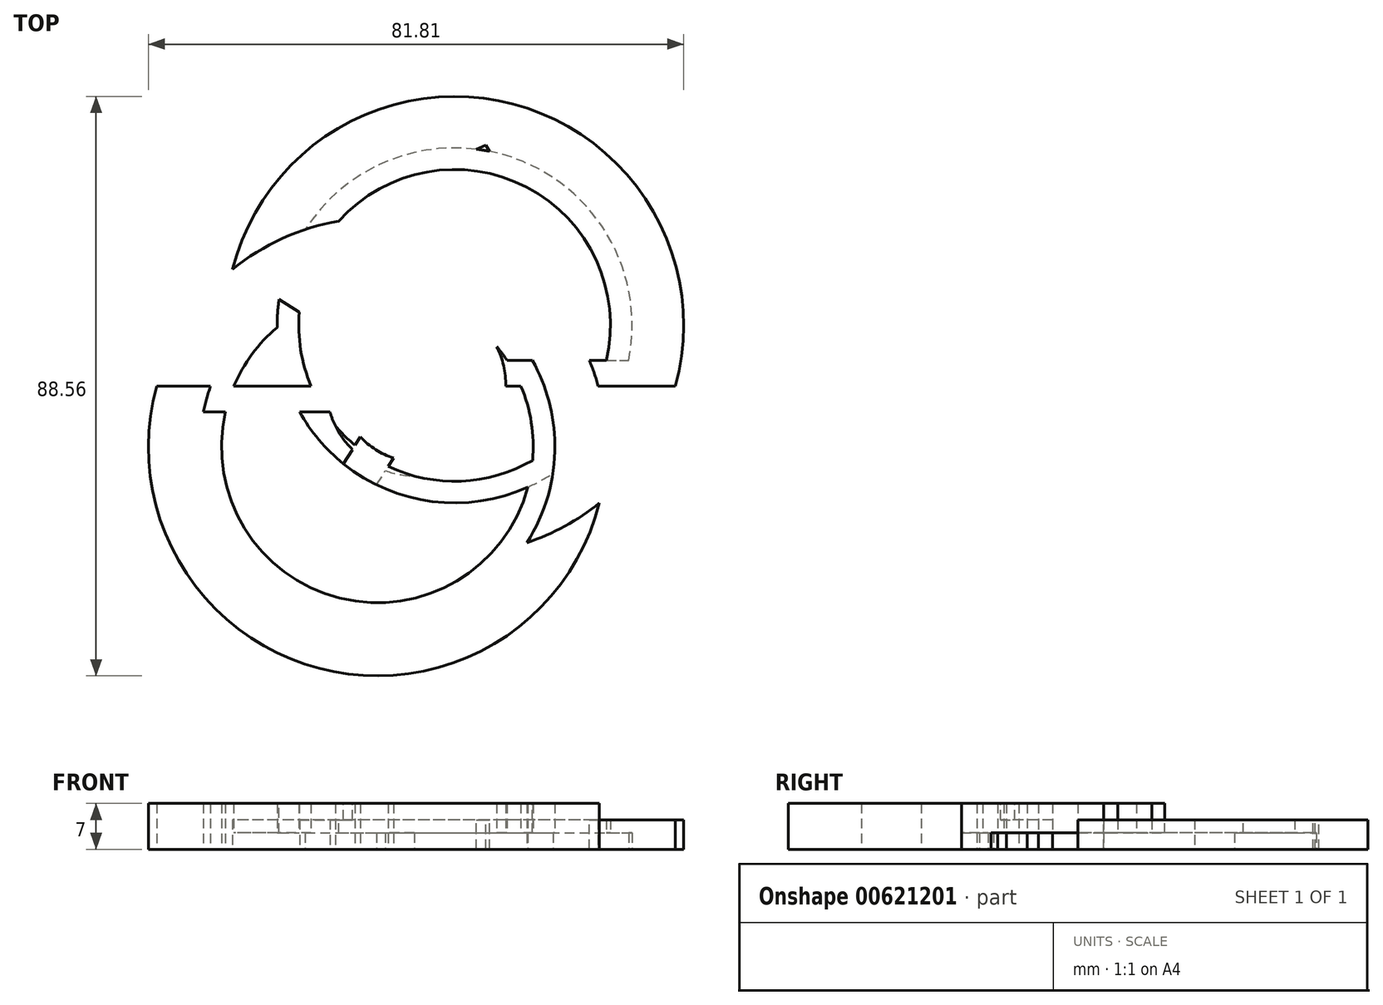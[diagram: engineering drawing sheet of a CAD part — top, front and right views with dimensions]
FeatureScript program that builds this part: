
annotation { "Feature Type Name" : "Feature", "Feature Type Description" : "" }
export const myFeature = defineFeature(function(context is Context, id is Id, definition is map)
    precondition{}
    {
        {
            var Q0;
            Q0=qCreatedBy(makeId("Top.planeOp"),FACE);
            var sketch = newSketch(context, id + "F0", { "sketchPlane" : qUnion([Q0])});
            skLineSegment(sketch, "E0", {"start": v(-39.07, 0) * mm, "end": v(40.23, 0) * mm});
            skPoint(sketch, "E1", {"position": v(0.58, 0) * mm});
            skPoint(sketch, "E2", {"position": v(11.92, 0) * mm});
            skPoint(sketch, "E3", {"position": v(-10.76, 0) * mm});
            skPoint(sketch, "E4", {"position": v(-22.57, 0) * mm});
            skArc(sketch, "E5", {"start": v(28.42, 0) * mm, "mid": v(-5.33, 25.72) * mm, "end": v(-39.07, 0) * mm});
            skLineSegment(sketch, "E6", {"start": v(28.42, 3.92) * mm, "end": v(40.23, 3.92) * mm});
            skPoint(sketch, "E7", {"position": v(34.32, 0) * mm});
            skPoint(sketch, "E7.positionSnap0", {"position": v(34.32, 3.92) * mm});
            skPoint(sketch, "E8", {"position": v(-30.82, 0) * mm});
            skPoint(sketch, "E9", {"position": v(-16.67, 0) * mm});
            skLineSegment(sketch, "E10", {"start": v(28.42, 3.92) * mm, "end": v(11.92, 3.92) * mm});
            skPoint(sketch, "E11", {"position": v(20.17, 0) * mm});
            skPoint(sketch, "E11.positionSnap0", {"position": v(20.17, 3.92) * mm});
            skArc(sketch, "E12", {"start": v(20.17, 0) * mm, "mid": v(-5.33, 17.85) * mm, "end": v(-30.82, 0) * mm});
            skLineSegment(sketch, "E13", {"start": v(40.23, 0) * mm, "end": v(-39.07, 0) * mm});
            skPoint(sketch, "E14", {"position": v(-27.27, 0) * mm});
            skPoint(sketch, "E15", {"position": v(23.72, 0) * mm});
            skArc(sketch, "E16", {"start": v(-27.27, 0) * mm, "mid": v(6.48, -25.72) * mm, "end": v(40.23, 0) * mm});
            skLineSegment(sketch, "E17", {"start": v(-27.27, -3.92) * mm, "end": v(-39.07, -3.92) * mm});
            skPoint(sketch, "E18", {"position": v(-33.17, 0) * mm});
            skPoint(sketch, "E18.positionSnap0", {"position": v(-33.17, -3.92) * mm});
            skPoint(sketch, "E19", {"position": v(31.98, 0) * mm});
            skPoint(sketch, "E20", {"position": v(24.15, -22) * mm});
            skLineSegment(sketch, "E21", {"start": v(-27.27, -3.92) * mm, "end": v(-10.76, -3.92) * mm});
            skPoint(sketch, "E22", {"position": v(-19.01, 0) * mm});
            skPoint(sketch, "E22.positionSnap0", {"position": v(-19.01, -3.92) * mm});
            skArc(sketch, "E23", {"start": v(-19.01, 0) * mm, "mid": v(6.48, -17.85) * mm, "end": v(31.98, 0) * mm});
            skCircle(sketch, "E24", {"center": v(6.48, 9.28) * mm, "radius": 27.13 * mm});
            skCircle(sketch, "E25", {"center": v(-5.33, -9.28) * mm, "radius": 27.13 * mm});
            skCircle(sketch, "E26", {"center": v(6.48, 9.28) * mm, "radius": 35 * mm});
            skCircle(sketch, "E27", {"center": v(-5.33, -9.28) * mm, "radius": 35 * mm});
            skLineSegment(sketch, "E28", {"start": v(0.58, 0) * mm, "end": v(-5.33, -9.28) * mm});
            skLineSegment(sketch, "E29", {"start": v(0.58, 0) * mm, "end": v(5.05, 7.03) * mm});
            skLineSegment(sketch, "E30", {"start": v(9.24, 13.61) * mm, "end": v(15.3, 9.75) * mm});
            skLineSegment(sketch, "E31", {"start": v(9.24, 13.61) * mm, "end": v(0.7, 19.04) * mm});
            skLineSegment(sketch, "E32", {"start": v(6.7, 15.22) * mm, "end": v(11.77, 12) * mm});
            skPoint(sketch, "E33", {"position": v(9.24, 13.61) * mm});
            skLineSegment(sketch, "E34", {"start": v(6.7, 15.22) * mm, "end": v(-10.53, -11.86) * mm});
            skLineSegment(sketch, "E35", {"start": v(11.77, 12) * mm, "end": v(-5.46, -15.08) * mm});
            skPoint(sketch, "E36", {"position": v(7.95, 11.59) * mm});
            skCircle(sketch, "E37", {"center": v(0.58, 0) * mm, "radius": 13.74 * mm});
            skCircle(sketch, "E38", {"center": v(-5.33, -9.28) * mm, "radius": 23.82 * mm});
            skCircle(sketch, "E39", {"center": v(6.48, 9.28) * mm, "radius": 23.82 * mm});
            skCircle(sketch, "E40", {"center": v(0.58, 0) * mm, "radius": 11.5 * mm});
            skSolve(sketch);
        }
        {
            var Q0;
            {var subQ0=sQuery(id+"F0.wireOp",EDGE,"E27");var subQ1=sQuery(id+"F0.wireOp",EDGE,"E13");var subQ2=makeQuery(id+"F0.imprint","INTERSECT",VERTEX,{"disambiguationData":[OD(0.0)],"derivedFrom":[subQ1,subQ0]});Q0=makeQuery(id+"F0.imprint","IMPRINT",FACE,{"disambiguationData":[TD([[makeQuery(id+"F0.imprint","IMPRINT",EDGE,{"disambiguationData":[TD([[subQ2,1.0]])],"derivedFrom":subQ1}),-1.0]])]});}
            var Q1;
            {var subQ0=sQuery(id+"F0.wireOp",EDGE,"E25");var subQ1=sQuery(id+"F0.wireOp",EDGE,"E24");var subQ2=makeQuery(id+"F0.imprint","INTERSECT",VERTEX,{"disambiguationData":[OD(0.0)],"derivedFrom":[subQ1,subQ0]});Q1=makeQuery(id+"F0.imprint","IMPRINT",FACE,{"disambiguationData":[TD([[makeQuery(id+"F0.imprint","IMPRINT",EDGE,{"disambiguationData":[TD([[subQ2,1.0]])],"derivedFrom":subQ1}),-1.0]])]});}
            var Q2;
            {var subQ0=sQuery(id+"F0.wireOp",EDGE,"E25");var subQ1=sQuery(id+"F0.wireOp",EDGE,"E24");var subQ2=makeQuery(id+"F0.imprint","INTERSECT",VERTEX,{"disambiguationData":[OD(1.0)],"derivedFrom":[subQ1,subQ0]});Q2=makeQuery(id+"F0.imprint","IMPRINT",FACE,{"disambiguationData":[TD([[makeQuery(id+"F0.imprint","IMPRINT",EDGE,{"disambiguationData":[TD([[subQ2,-1.0]])],"derivedFrom":subQ1}),-1.0]])]});}
            var Q3;
            {var subQ0=sQuery(id+"F0.wireOp",EDGE,"E27");var subQ1=sQuery(id+"F0.wireOp",EDGE,"E13");var subQ2=makeQuery(id+"F0.imprint","INTERSECT",VERTEX,{"disambiguationData":[OD(1.0)],"derivedFrom":[subQ1,subQ0]});Q3=makeQuery(id+"F0.imprint","IMPRINT",FACE,{"disambiguationData":[TD([[makeQuery(id+"F0.imprint","IMPRINT",EDGE,{"disambiguationData":[TD([[subQ2,-1.0]])],"derivedFrom":subQ1}),1.0]])]});}
            var Q4;
            {var subQ1=sQuery(id+"F0.wireOp",EDGE,"E10");var subQ7=sQuery(id+"F0.wireOp",EDGE,"E27");var subQ14=makeQuery(id+"F0.imprint","INTERSECT",VERTEX,{"derivedFrom":[subQ1,subQ7]});Q4=makeQuery(id+"F0.imprint","IMPRINT",FACE,{"disambiguationData":[TD([[makeQuery(id+"F0.imprint","IMPRINT",EDGE,{"disambiguationData":[TD([[subQ14,-1.0]])],"derivedFrom":subQ1}),-1.0]])]});}
            var Q5;
            {var subQ0=sQuery(id+"F0.wireOp",EDGE,"E27");var subQ1=sQuery(id+"F0.wireOp",EDGE,"E10");var subQ2=makeQuery(id+"F0.imprint","INTERSECT",VERTEX,{"derivedFrom":[subQ1,subQ0]});Q5=makeQuery(id+"F0.imprint","IMPRINT",FACE,{"disambiguationData":[TD([[makeQuery(id+"F0.imprint","IMPRINT",EDGE,{"disambiguationData":[TD([[subQ2,-1.0]])],"derivedFrom":subQ1}),1.0]])]});}
            var Q6;
            {var subQ5=sQuery(id+"F0.wireOp",EDGE,"E21");var subQ7=sQuery(id+"F0.wireOp",EDGE,"E26");var subQ8=makeQuery(id+"F0.imprint","INTERSECT",VERTEX,{"derivedFrom":[subQ5,subQ7]});Q6=makeQuery(id+"F0.imprint","IMPRINT",FACE,{"disambiguationData":[TD([[makeQuery(id+"F0.imprint","IMPRINT",EDGE,{"disambiguationData":[TD([[subQ8,-1.0]])],"derivedFrom":subQ5}),-1.0]])]});}
            var Q7;
            {var subQ0=sQuery(id+"F0.wireOp",EDGE,"E24");var subQ1=sQuery(id+"F0.wireOp",EDGE,"E13");var subQ2=makeQuery(id+"F0.imprint","INTERSECT",VERTEX,{"disambiguationData":[OD(1.0)],"derivedFrom":[subQ1,subQ0]});Q7=makeQuery(id+"F0.imprint","IMPRINT",FACE,{"disambiguationData":[TD([[makeQuery(id+"F0.imprint","IMPRINT",EDGE,{"disambiguationData":[TD([[subQ2,-1.0]])],"derivedFrom":subQ1}),1.0]])]});}
            var Q8;
            {var subQ0=sQuery(id+"F0.wireOp",EDGE,"E24");var subQ1=sQuery(id+"F0.wireOp",EDGE,"E13");var subQ2=makeQuery(id+"F0.imprint","INTERSECT",VERTEX,{"disambiguationData":[OD(1.0)],"derivedFrom":[subQ1,subQ0]});Q8=makeQuery(id+"F0.imprint","IMPRINT",FACE,{"disambiguationData":[TD([[makeQuery(id+"F0.imprint","IMPRINT",EDGE,{"disambiguationData":[TD([[subQ2,-1.0]])],"derivedFrom":subQ1}),-1.0]])]});}
            var Q9;
            {var subQ0=sQuery(id+"F0.wireOp",EDGE,"E26");var subQ1=sQuery(id+"F0.wireOp",EDGE,"E13");var subQ2=makeQuery(id+"F0.imprint","INTERSECT",VERTEX,{"disambiguationData":[OD(0.0)],"derivedFrom":[subQ1,subQ0]});Q9=makeQuery(id+"F0.imprint","IMPRINT",FACE,{"disambiguationData":[TD([[makeQuery(id+"F0.imprint","IMPRINT",EDGE,{"disambiguationData":[TD([[subQ2,-1.0]])],"derivedFrom":subQ1}),1.0]])]});}
            var Q10;
            {var subQ0=sQuery(id+"F0.wireOp",EDGE,"E25");var subQ1=sQuery(id+"F0.wireOp",EDGE,"E24");var subQ2=makeQuery(id+"F0.imprint","INTERSECT",VERTEX,{"disambiguationData":[OD(0.0)],"derivedFrom":[subQ1,subQ0]});Q10=makeQuery(id+"F0.imprint","IMPRINT",FACE,{"disambiguationData":[TD([[makeQuery(id+"F0.imprint","IMPRINT",EDGE,{"disambiguationData":[TD([[subQ2,1.0]])],"derivedFrom":subQ1}),1.0]])]});}
            var Q11;
            {var subQ0=sQuery(id+"F0.wireOp",EDGE,"E25");var subQ1=sQuery(id+"F0.wireOp",EDGE,"E24");var subQ2=makeQuery(id+"F0.imprint","INTERSECT",VERTEX,{"disambiguationData":[OD(0.0)],"derivedFrom":[subQ1,subQ0]});Q11=makeQuery(id+"F0.imprint","IMPRINT",FACE,{"disambiguationData":[TD([[makeQuery(id+"F0.imprint","IMPRINT",EDGE,{"disambiguationData":[TD([[subQ2,-1.0]])],"derivedFrom":subQ1}),-1.0]])]});}
            var Q12;
            {var subQ0=sQuery(id+"F0.wireOp",EDGE,"E25");var subQ1=sQuery(id+"F0.wireOp",EDGE,"E13");var subQ2=makeQuery(id+"F0.imprint","INTERSECT",VERTEX,{"disambiguationData":[OD(0.0)],"derivedFrom":[subQ1,subQ0]});Q12=makeQuery(id+"F0.imprint","IMPRINT",FACE,{"disambiguationData":[TD([[makeQuery(id+"F0.imprint","IMPRINT",EDGE,{"disambiguationData":[TD([[subQ2,1.0]])],"derivedFrom":subQ0}),-1.0]])]});}
            var Q13;
            {var subQ0=sQuery(id+"F0.wireOp",EDGE,"E25");var subQ1=sQuery(id+"F0.wireOp",EDGE,"E24");var subQ2=makeQuery(id+"F0.imprint","INTERSECT",VERTEX,{"disambiguationData":[OD(1.0)],"derivedFrom":[subQ1,subQ0]});Q13=makeQuery(id+"F0.imprint","IMPRINT",FACE,{"disambiguationData":[TD([[makeQuery(id+"F0.imprint","IMPRINT",EDGE,{"disambiguationData":[TD([[subQ2,-1.0]])],"derivedFrom":subQ1}),1.0]])]});}
            var Q14;
            {var subQ0=sQuery(id+"F0.wireOp",EDGE,"E38");var subQ1=sQuery(id+"F0.wireOp",EDGE,"E24");var subQ2=makeQuery(id+"F0.imprint","INTERSECT",VERTEX,{"disambiguationData":[OD(1.0)],"derivedFrom":[subQ1,subQ0]});Q14=makeQuery(id+"F0.imprint","IMPRINT",FACE,{"disambiguationData":[TD([[makeQuery(id+"F0.imprint","IMPRINT",EDGE,{"disambiguationData":[TD([[subQ2,-1.0]])],"derivedFrom":subQ1}),-1.0]])]});}
            extrude(context, id + "F1", {"entities" : qUnion([Q0, Q1, Q2, Q3, Q4, Q5, Q6, Q7, Q8, Q9, Q10, Q11, Q12, Q13, Q14]), "depth" : 7 * mm, "offsetDistance" : 25 * mm});
        }
        {
            var Q0;
            {var subQ0=sQuery(id+"F0.wireOp",EDGE,"E35");var subQ1=sQuery(id+"F0.wireOp",EDGE,"E25");var subQ2=makeQuery(id+"F0.imprint","INTERSECT",VERTEX,{"derivedFrom":[subQ1,subQ0]});Q0=makeQuery(id+"F0.imprint","IMPRINT",FACE,{"disambiguationData":[TD([[makeQuery(id+"F0.imprint","IMPRINT",EDGE,{"disambiguationData":[TD([[subQ2,-1.0]])],"derivedFrom":subQ1}),1.0]])]});}
            var Q1;
            {var subQ0=sQuery(id+"F0.wireOp",EDGE,"E35");var subQ1=sQuery(id+"F0.wireOp",EDGE,"7e9791cb-aaaf-4d6e-a51d-a6ec5d2c7f44");var subQ2=makeQuery(id+"F0.imprint","INTERSECT",VERTEX,{"disambiguationData":[OD(1.0)],"derivedFrom":[subQ1,subQ0]});Q1=makeQuery(id+"F0.imprint","IMPRINT",FACE,{"disambiguationData":[TD([[makeQuery(id+"F0.imprint","IMPRINT",EDGE,{"disambiguationData":[TD([[subQ2,-1.0]])],"derivedFrom":subQ1}),-1.0]])]});}
            var Q2;
            {var subQ0=sQuery(id+"F0.wireOp",EDGE,"E37");var subQ2=sQuery(id+"F0.wireOp",EDGE,"E13");var subQ3=makeQuery(id+"F0.imprint","INTERSECT",VERTEX,{"disambiguationData":[OD(0.0)],"derivedFrom":[subQ2,subQ0]});Q2=makeQuery(id+"F0.imprint","IMPRINT",FACE,{"disambiguationData":[TD([[makeQuery(id+"F0.imprint","IMPRINT",EDGE,{"disambiguationData":[TD([[subQ3,-1.0]])],"derivedFrom":subQ2}),-1.0]])]});}
            var Q3;
            {var subQ0=sQuery(id+"F0.wireOp",EDGE,"E37");var subQ1=sQuery(id+"F0.wireOp",EDGE,"E13");var subQ2=makeQuery(id+"F0.imprint","INTERSECT",VERTEX,{"disambiguationData":[OD(0.0)],"derivedFrom":[subQ1,subQ0]});Q3=makeQuery(id+"F0.imprint","IMPRINT",FACE,{"disambiguationData":[TD([[makeQuery(id+"F0.imprint","IMPRINT",EDGE,{"disambiguationData":[TD([[subQ2,-1.0]])],"derivedFrom":subQ1}),1.0]])]});}
            var Q4;
            {var subQ0=sQuery(id+"F0.wireOp",EDGE,"7e9791cb-aaaf-4d6e-a51d-a6ec5d2c7f44");var subQ1=sQuery(id+"F0.wireOp",EDGE,"E13");var subQ2=makeQuery(id+"F0.imprint","INTERSECT",VERTEX,{"disambiguationData":[OD(1.0)],"derivedFrom":[subQ1,subQ0]});Q4=makeQuery(id+"F0.imprint","IMPRINT",FACE,{"disambiguationData":[TD([[makeQuery(id+"F0.imprint","IMPRINT",EDGE,{"disambiguationData":[TD([[subQ2,-1.0]])],"derivedFrom":subQ1}),-1.0]])]});}
            var Q5;
            {var subQ1=sQuery(id+"F0.wireOp",EDGE,"7e9791cb-aaaf-4d6e-a51d-a6ec5d2c7f44");var subQ6=sQuery(id+"F0.wireOp",EDGE,"E13");var subQ8=makeQuery(id+"F0.imprint","INTERSECT",VERTEX,{"disambiguationData":[OD(1.0)],"derivedFrom":[subQ6,subQ1]});Q5=makeQuery(id+"F0.imprint","IMPRINT",FACE,{"disambiguationData":[TD([[makeQuery(id+"F0.imprint","IMPRINT",EDGE,{"disambiguationData":[TD([[subQ8,-1.0]])],"derivedFrom":subQ6}),1.0]])]});}
            var Q6;
            {var subQ0=sQuery(id+"F0.wireOp",EDGE,"E34");var subQ1=sQuery(id+"F0.wireOp",EDGE,"7e9791cb-aaaf-4d6e-a51d-a6ec5d2c7f44");var subQ2=makeQuery(id+"F0.imprint","INTERSECT",VERTEX,{"disambiguationData":[OD(0.0)],"derivedFrom":[subQ1,subQ0]});Q6=makeQuery(id+"F0.imprint","IMPRINT",FACE,{"disambiguationData":[TD([[makeQuery(id+"F0.imprint","IMPRINT",EDGE,{"disambiguationData":[TD([[subQ2,-1.0]])],"derivedFrom":subQ1}),-1.0]])]});}
            var Q7;
            {var subQ0=sQuery(id+"F0.wireOp",EDGE,"E34");var subQ1=sQuery(id+"F0.wireOp",EDGE,"E24");var subQ2=makeQuery(id+"F0.imprint","INTERSECT",VERTEX,{"derivedFrom":[subQ1,subQ0]});Q7=makeQuery(id+"F0.imprint","IMPRINT",FACE,{"disambiguationData":[TD([[makeQuery(id+"F0.imprint","IMPRINT",EDGE,{"disambiguationData":[TD([[subQ2,-1.0]])],"derivedFrom":subQ1}),1.0]])]});}
            var Q8;
            {var subQ0=sQuery(id+"F0.wireOp",EDGE,"E32");var subQ1=sQuery(id+"F0.wireOp",EDGE,"E25");var subQ2=makeQuery(id+"F0.imprint","INTERSECT",VERTEX,{"derivedFrom":[subQ1,subQ0]});Q8=makeQuery(id+"F0.imprint","IMPRINT",FACE,{"disambiguationData":[TD([[makeQuery(id+"F0.imprint","IMPRINT",EDGE,{"disambiguationData":[TD([[subQ2,-1.0]])],"derivedFrom":subQ1}),-1.0]])]});}
            var Q9;
            {var subQ0=sQuery(id+"F0.wireOp",EDGE,"E35");var subQ1=sQuery(id+"F0.wireOp",EDGE,"E25");var subQ2=makeQuery(id+"F0.imprint","INTERSECT",VERTEX,{"derivedFrom":[subQ1,subQ0]});Q9=makeQuery(id+"F0.imprint","IMPRINT",FACE,{"disambiguationData":[TD([[makeQuery(id+"F0.imprint","IMPRINT",EDGE,{"disambiguationData":[TD([[subQ2,-1.0]])],"derivedFrom":subQ1}),-1.0]])]});}
            var Q10;
            {var subQ0=sQuery(id+"F0.wireOp",EDGE,"E39");var subQ1=sQuery(id+"F0.wireOp",EDGE,"E34");var subQ2=makeQuery(id+"F0.imprint","INTERSECT",VERTEX,{"derivedFrom":[subQ1,subQ0]});Q10=makeQuery(id+"F0.imprint","IMPRINT",FACE,{"disambiguationData":[TD([[makeQuery(id+"F0.imprint","IMPRINT",EDGE,{"disambiguationData":[TD([[subQ2,-1.0]])],"derivedFrom":subQ1}),1.0]])]});}
            var Q11;
            {var subQ0=sQuery(id+"F0.wireOp",EDGE,"E39");var subQ1=sQuery(id+"F0.wireOp",EDGE,"E35");var subQ2=makeQuery(id+"F0.imprint","INTERSECT",VERTEX,{"derivedFrom":[subQ1,subQ0]});Q11=makeQuery(id+"F0.imprint","IMPRINT",FACE,{"disambiguationData":[TD([[makeQuery(id+"F0.imprint","IMPRINT",EDGE,{"disambiguationData":[TD([[subQ2,-1.0]])],"derivedFrom":subQ1}),1.0]])]});}
            var Q12;
            {var subQ0=sQuery(id+"F0.wireOp",EDGE,"E39");var subQ1=sQuery(id+"F0.wireOp",EDGE,"E34");var subQ2=makeQuery(id+"F0.imprint","INTERSECT",VERTEX,{"derivedFrom":[subQ1,subQ0]});Q12=makeQuery(id+"F0.imprint","IMPRINT",FACE,{"disambiguationData":[TD([[makeQuery(id+"F0.imprint","IMPRINT",EDGE,{"disambiguationData":[TD([[subQ2,-1.0]])],"derivedFrom":subQ1}),-1.0]])]});}
            var Q13;
            {var subQ0=sQuery(id+"F0.wireOp",EDGE,"E37");var subQ1=sQuery(id+"F0.wireOp",EDGE,"E34");var subQ2=makeQuery(id+"F0.imprint","INTERSECT",VERTEX,{"disambiguationData":[OD(0.0)],"derivedFrom":[subQ1,subQ0]});Q13=makeQuery(id+"F0.imprint","IMPRINT",FACE,{"disambiguationData":[TD([[makeQuery(id+"F0.imprint","IMPRINT",EDGE,{"disambiguationData":[TD([[subQ2,-1.0]])],"derivedFrom":subQ1}),1.0]])]});}
            var Q14;
            {var subQ0=sQuery(id+"F0.wireOp",EDGE,"E37");var subQ1=sQuery(id+"F0.wireOp",EDGE,"E35");var subQ2=makeQuery(id+"F0.imprint","INTERSECT",VERTEX,{"disambiguationData":[OD(0.0)],"derivedFrom":[subQ1,subQ0]});Q14=makeQuery(id+"F0.imprint","IMPRINT",FACE,{"disambiguationData":[TD([[makeQuery(id+"F0.imprint","IMPRINT",EDGE,{"disambiguationData":[TD([[subQ2,-1.0]])],"derivedFrom":subQ1}),1.0]])]});}
            var Q15;
            {var subQ0=sQuery(id+"F0.wireOp",EDGE,"E37");var subQ1=sQuery(id+"F0.wireOp",EDGE,"E34");var subQ2=makeQuery(id+"F0.imprint","INTERSECT",VERTEX,{"disambiguationData":[OD(0.0)],"derivedFrom":[subQ1,subQ0]});Q15=makeQuery(id+"F0.imprint","IMPRINT",FACE,{"disambiguationData":[TD([[makeQuery(id+"F0.imprint","IMPRINT",EDGE,{"disambiguationData":[TD([[subQ2,-1.0]])],"derivedFrom":subQ1}),-1.0]])]});}
            var Q16;
            {var subQ2=sQuery(id+"F0.wireOp",EDGE,"E13");var subQ4=sQuery(id+"F0.wireOp",EDGE,"E40");var subQ10=makeQuery(id+"F0.imprint","INTERSECT",VERTEX,{"disambiguationData":[OD(1.0)],"derivedFrom":[subQ2,subQ4]});Q16=makeQuery(id+"F0.imprint","IMPRINT",FACE,{"disambiguationData":[TD([[makeQuery(id+"F0.imprint","IMPRINT",EDGE,{"disambiguationData":[TD([[subQ10,-1.0]])],"derivedFrom":subQ2}),1.0]])]});}
            var Q17;
            {var subQ0=sQuery(id+"F0.wireOp",EDGE,"E40");var subQ1=sQuery(id+"F0.wireOp",EDGE,"E34");var subQ2=makeQuery(id+"F0.imprint","INTERSECT",VERTEX,{"disambiguationData":[OD(1.0)],"derivedFrom":[subQ1,subQ0]});Q17=makeQuery(id+"F0.imprint","IMPRINT",FACE,{"disambiguationData":[TD([[makeQuery(id+"F0.imprint","IMPRINT",EDGE,{"disambiguationData":[TD([[subQ2,-1.0]])],"derivedFrom":subQ1}),1.0]])]});}
            var Q18;
            {var subQ5=sQuery(id+"F0.wireOp",EDGE,"E13");var subQ7=sQuery(id+"F0.wireOp",EDGE,"E40");var subQ9=makeQuery(id+"F0.imprint","INTERSECT",VERTEX,{"disambiguationData":[OD(1.0)],"derivedFrom":[subQ5,subQ7]});Q18=makeQuery(id+"F0.imprint","IMPRINT",FACE,{"disambiguationData":[TD([[makeQuery(id+"F0.imprint","IMPRINT",EDGE,{"disambiguationData":[TD([[subQ9,-1.0]])],"derivedFrom":subQ5}),-1.0]])]});}
            var Q19;
            {var subQ0=sQuery(id+"F0.wireOp",EDGE,"E38");var subQ1=sQuery(id+"F0.wireOp",EDGE,"E34");var subQ2=makeQuery(id+"F0.imprint","INTERSECT",VERTEX,{"derivedFrom":[subQ1,subQ0]});Q19=makeQuery(id+"F0.imprint","IMPRINT",FACE,{"disambiguationData":[TD([[makeQuery(id+"F0.imprint","IMPRINT",EDGE,{"disambiguationData":[TD([[subQ2,-1.0]])],"derivedFrom":subQ1}),1.0]])]});}
            extrude(context, id + "F2", {"entities" : qUnion([Q0, Q1, Q2, Q3, Q4, Q5, Q6, Q7, Q8, Q9, Q10, Q11, Q12, Q13, Q14, Q15, Q16, Q17, Q18, Q19]), "operationType" : NewBodyOperationType.ADD, "depth" : 7 * mm, "offsetDistance" : 25 * mm});
        }
        {
            var Q0;
            {var subQ0=sQuery(id+"F0.wireOp",EDGE,"E35");var subQ1=sQuery(id+"F0.wireOp",EDGE,"E34");var subQ2=sQuery(id+"F0.wireOp",EDGE,"E32");var subQ3=sQuery(id+"F0.wireOp",EDGE,"E24");Q0=makeQuery(id+"F2.boolean.opBoolean","MERGE",FACE,{"derivedFrom":[makeQuery(id+"F1.opExtrude","CAP_FACE",FACE,{"disambiguationData":[OSD([sQuery(id+"F0.wireOp",EDGE,"E13"),subQ3,sQuery(id+"F0.wireOp",EDGE,"E25"),sQuery(id+"F0.wireOp",EDGE,"E26"),sQuery(id+"F0.wireOp",EDGE,"E27"),subQ2,subQ1,subQ0])],"isStart":false}),makeQuery(id+"F2.opExtrude","CAP_FACE",FACE,{"disambiguationData":[OSD([sQuery(id+"F0.wireOp",EDGE,"7e9791cb-aaaf-4d6e-a51d-a6ec5d2c7f44"),subQ3,subQ2,subQ1,subQ0,sQuery(id+"F0.wireOp",EDGE,"E37")])],"isStart":false})]});}
            var sketch = newSketch(context, id + "F3", { "sketchPlane" : qUnion([Q0])});
            skLineSegment(sketch, "E41", {"start": v(6.62, 15.08) * mm, "end": v(5.24, 12.92) * mm});
            skLineSegment(sketch, "E42", {"start": v(11.68, 11.86) * mm, "end": v(10.3, 9.7) * mm});
            skLineSegment(sketch, "E43", {"start": v(-10.53, -11.86) * mm, "end": v(-9.15, -9.7) * mm});
            skLineSegment(sketch, "E44", {"start": v(-4.09, -12.92) * mm, "end": v(-5.46, -15.08) * mm});
            skPoint(sketch, "E45", {"position": v(8.71, 7.9) * mm});
            skPoint(sketch, "E46", {"position": v(10.8, 9.17) * mm});
            skCircle(sketch, "E47", {"center": v(0.58, 0) * mm, "radius": 13.74 * mm});
            skCircle(sketch, "E48", {"center": v(6.48, 9.28) * mm, "radius": 27.13 * mm});
            skCircle(sketch, "E49", {"center": v(-5.33, -9.28) * mm, "radius": 27.13 * mm});
            skCircle(sketch, "E50", {"center": v(0.58, 0) * mm, "radius": 11.5 * mm});
            skSolve(sketch);
        }
        {
            var Q0;
            {var subQ0=sQuery(id+"F3.wireOp",EDGE,"E41");Q0=makeQuery(id+"F3.imprint","IMPRINT",FACE,{"disambiguationData":[TD([[makeQuery(id+"F3.imprint","IMPRINT",EDGE,{"derivedFrom":subQ0}),1.0]])]});}
            var Q1;
            {var subQ0=sQuery(id+"F3.wireOp",EDGE,"E43");Q1=makeQuery(id+"F3.imprint","IMPRINT",FACE,{"disambiguationData":[TD([[makeQuery(id+"F3.imprint","IMPRINT",EDGE,{"derivedFrom":subQ0}),1.0]])]});}
            extrude(context, id + "F4", {"entities" : qUnion([Q0, Q1]), "operationType" : NewBodyOperationType.REMOVE, "oppositeDirection" : true, "depth" : 2.5 * mm, "offsetDistance" : 25 * mm});
        }
        {
            var Q0;
            {var subQ0=sQuery(id+"F0.wireOp",EDGE,"E35");var subQ1=sQuery(id+"F0.wireOp",EDGE,"E34");var subQ2=sQuery(id+"F0.wireOp",EDGE,"E32");var subQ3=sQuery(id+"F0.wireOp",EDGE,"E24");Q0=makeQuery(id+"F2.boolean.opBoolean","MERGE",FACE,{"derivedFrom":[makeQuery(id+"F1.opExtrude","CAP_FACE",FACE,{"disambiguationData":[OSD([sQuery(id+"F0.wireOp",EDGE,"E13"),subQ3,sQuery(id+"F0.wireOp",EDGE,"E25"),sQuery(id+"F0.wireOp",EDGE,"E26"),sQuery(id+"F0.wireOp",EDGE,"E27"),subQ2,subQ1,subQ0])],"isStart":true}),makeQuery(id+"F2.opExtrude","CAP_FACE",FACE,{"disambiguationData":[OSD([sQuery(id+"F0.wireOp",EDGE,"7e9791cb-aaaf-4d6e-a51d-a6ec5d2c7f44"),subQ3,subQ2,subQ1,subQ0,sQuery(id+"F0.wireOp",EDGE,"E37")])],"isStart":true})]});}
            var sketch = newSketch(context, id + "F5", { "sketchPlane" : qUnion([Q0])});
            skLineSegment(sketch, "E51", {"start": v(-10.53, 11.86) * mm, "end": v(-7.82, 7.61) * mm});
            skLineSegment(sketch, "E52", {"start": v(-5.46, 15.08) * mm, "end": v(-4.09, 12.92) * mm});
            skLineSegment(sketch, "E53", {"start": v(5.24, -12.92) * mm, "end": v(6.62, -15.08) * mm});
            skLineSegment(sketch, "E54", {"start": v(11.68, -11.86) * mm, "end": v(10.3, -9.7) * mm});
            skCircle(sketch, "E55", {"center": v(0.58, 0) * mm, "radius": 13.74 * mm});
            skCircle(sketch, "E56", {"center": v(6.48, -9.28) * mm, "radius": 27.13 * mm});
            skCircle(sketch, "E57", {"center": v(-5.33, 9.28) * mm, "radius": 27.13 * mm});
            skSolve(sketch);
        }
        {
            var Q0;
            {var subQ27=sQuery(id+"F5.wireOp",EDGE,"E52");Q0=makeQuery(id+"F5.imprint","IMPRINT",FACE,{"disambiguationData":[TD([[makeQuery(id+"F5.imprint","IMPRINT",EDGE,{"derivedFrom":subQ27}),1.0]])]});}
            var Q1;
            {var subQ0=sQuery(id+"F5.wireOp",EDGE,"E53");Q1=makeQuery(id+"F5.imprint","IMPRINT",FACE,{"disambiguationData":[TD([[makeQuery(id+"F5.imprint","IMPRINT",EDGE,{"derivedFrom":subQ0}),-1.0]])]});}
            var Q2;
            {var subQ0=sQuery(id+"F0.wireOp",EDGE,"E34");var subQ1=sQuery(id+"F0.wireOp",EDGE,"E24");var subQ2=makeQuery(id+"F0.imprint","INTERSECT",VERTEX,{"derivedFrom":[subQ1,subQ0]});Q2=makeQuery(id+"F0.imprint","IMPRINT",FACE,{"disambiguationData":[TD([[makeQuery(id+"F0.imprint","IMPRINT",EDGE,{"disambiguationData":[TD([[subQ2,-1.0]])],"derivedFrom":subQ1}),1.0]])]});}
            extrude(context, id + "F6", {"entities" : qUnion([Q0, Q1, Q2]), "operationType" : NewBodyOperationType.REMOVE, "oppositeDirection" : true, "depth" : 2.5 * mm, "offsetDistance" : 25 * mm});
        }
        {
            var Q0;
            {var subQ0=sQuery(id+"F0.wireOp",EDGE,"E27");var subQ1=sQuery(id+"F0.wireOp",EDGE,"E26");var subQ2=sQuery(id+"F0.wireOp",EDGE,"E25");var subQ3=sQuery(id+"F0.wireOp",EDGE,"E13");var subQ5=sQuery(id+"F0.wireOp",EDGE,"E24");var subQ9=sQuery(id+"F0.wireOp",EDGE,"E34");var subQ13=sQuery(id+"F0.wireOp",EDGE,"E35");var subQ23=sQuery(id+"F0.wireOp",EDGE,"E32");Q0=makeQuery(id+"F6.boolean.opBoolean","SPLIT",FACE,{"disambiguationData":[TD([makeQuery(id+"F1.opExtrude","SWEPT_FACE",FACE,{"disambiguationData":[OSD([subQ1])]})])],"derivedFrom":makeQuery(id+"F2.boolean.opBoolean","MERGE",FACE,{"derivedFrom":[makeQuery(id+"F1.opExtrude","CAP_FACE",FACE,{"disambiguationData":[OSD([subQ3,subQ5,subQ2,subQ1,subQ0,subQ23,subQ9,subQ13])],"isStart":true}),makeQuery(id+"F2.opExtrude","CAP_FACE",FACE,{"disambiguationData":[OSD([sQuery(id+"F0.wireOp",EDGE,"7e9791cb-aaaf-4d6e-a51d-a6ec5d2c7f44"),subQ5,subQ23,subQ9,subQ13,sQuery(id+"F0.wireOp",EDGE,"E37")])],"isStart":true})]})});}
            var sketch = newSketch(context, id + "F7", { "sketchPlane" : qUnion([Q0])});
            skSolve(sketch);
        }
        {
            var Q0;
            Q0 = qSketchRegion(id + "F7", true);
            var Q1;
            {var subQ0=sQuery(id+"F0.wireOp",EDGE,"E25");var subQ1=sQuery(id+"F0.wireOp",EDGE,"E24");var subQ2=makeQuery(id+"F0.imprint","INTERSECT",VERTEX,{"disambiguationData":[OD(0.0)],"derivedFrom":[subQ1,subQ0]});Q1=makeQuery(id+"F0.imprint","IMPRINT",FACE,{"disambiguationData":[TD([[makeQuery(id+"F0.imprint","IMPRINT",EDGE,{"disambiguationData":[TD([[subQ2,-1.0]])],"derivedFrom":subQ1}),-1.0]])]});}
            extrude(context, id + "F8", {"entities" : qUnion([Q0, Q1]), "operationType" : NewBodyOperationType.REMOVE, "depth" : 2.5 * mm, "offsetDistance" : 25 * mm});
        }
        {
            var Q0;
            {var subQ0=sQuery(id+"F0.wireOp",EDGE,"E27");var subQ1=sQuery(id+"F0.wireOp",EDGE,"E26");var subQ2=sQuery(id+"F0.wireOp",EDGE,"E25");var subQ3=sQuery(id+"F0.wireOp",EDGE,"E13");var subQ5=sQuery(id+"F0.wireOp",EDGE,"E24");var subQ9=sQuery(id+"F0.wireOp",EDGE,"E34");var subQ13=sQuery(id+"F0.wireOp",EDGE,"E35");var subQ23=sQuery(id+"F0.wireOp",EDGE,"E32");Q0=makeQuery(id+"F4.boolean.opBoolean","SPLIT",FACE,{"disambiguationData":[TD([makeQuery(id+"F1.opExtrude","SWEPT_FACE",FACE,{"disambiguationData":[OSD([subQ1])]})])],"derivedFrom":makeQuery(id+"F2.boolean.opBoolean","MERGE",FACE,{"derivedFrom":[makeQuery(id+"F1.opExtrude","CAP_FACE",FACE,{"disambiguationData":[OSD([subQ3,subQ5,subQ2,subQ1,subQ0,subQ23,subQ9,subQ13])],"isStart":false}),makeQuery(id+"F2.opExtrude","CAP_FACE",FACE,{"disambiguationData":[OSD([sQuery(id+"F0.wireOp",EDGE,"7e9791cb-aaaf-4d6e-a51d-a6ec5d2c7f44"),subQ5,subQ23,subQ9,subQ13,sQuery(id+"F0.wireOp",EDGE,"E37")])],"isStart":false})]})});}
            var sketch = newSketch(context, id + "F9", { "sketchPlane" : qUnion([Q0])});
            skCircle(sketch, "E58", {"center": v(-5.33, -9.28) * mm, "radius": 27.13 * mm});
            skPoint(sketch, "E59", {"position": v(-27.27, 0) * mm});
            skCircle(sketch, "E60", {"center": v(-5.33, -9.28) * mm, "radius": 23.82 * mm});
            skSolve(sketch);
        }
        {
            var Q0;
            {var subQ0=sQuery(id+"F9.wireOp",EDGE,"E58");var subQ30=sQuery(id+"F0.wireOp",EDGE,"E26");var subQ36=makeQuery(id+"F1.opExtrude","CAP_EDGE",EDGE,{"disambiguationData":[OSD([subQ30])],"isStart":false});var subQ37=makeQuery(id+"F9.imprint","INTERSECT",VERTEX,{"disambiguationData":[OD(0.0)],"derivedFrom":[subQ36,subQ0]});Q0=makeQuery(id+"F9.imprint","IMPRINT",FACE,{"disambiguationData":[TD([[makeQuery(id+"F9.imprint","IMPRINT",EDGE,{"disambiguationData":[TD([[subQ37,-1.0]])],"derivedFrom":subQ36}),1.0]])]});}
            extrude(context, id + "F10", {"entities" : qUnion([Q0]), "operationType" : NewBodyOperationType.REMOVE, "oppositeDirection" : true, "depth" : 2.5 * mm, "offsetDistance" : 25 * mm});
        }
        {
            var Q0;
            {var subQ0=sQuery(id+"F0.wireOp",EDGE,"E27");var subQ1=sQuery(id+"F0.wireOp",EDGE,"E26");var subQ2=sQuery(id+"F0.wireOp",EDGE,"E25");var subQ3=sQuery(id+"F0.wireOp",EDGE,"E13");var subQ5=sQuery(id+"F0.wireOp",EDGE,"E24");var subQ9=sQuery(id+"F0.wireOp",EDGE,"E34");var subQ13=sQuery(id+"F0.wireOp",EDGE,"E35");var subQ23=sQuery(id+"F0.wireOp",EDGE,"E32");Q0=makeQuery(id+"F4.boolean.opBoolean","SPLIT",FACE,{"disambiguationData":[TD([makeQuery(id+"F1.opExtrude","SWEPT_FACE",FACE,{"disambiguationData":[OSD([subQ1])]})])],"derivedFrom":makeQuery(id+"F2.boolean.opBoolean","MERGE",FACE,{"derivedFrom":[makeQuery(id+"F1.opExtrude","CAP_FACE",FACE,{"disambiguationData":[OSD([subQ3,subQ5,subQ2,subQ1,subQ0,subQ23,subQ9,subQ13])],"isStart":false}),makeQuery(id+"F2.opExtrude","CAP_FACE",FACE,{"disambiguationData":[OSD([sQuery(id+"F0.wireOp",EDGE,"7e9791cb-aaaf-4d6e-a51d-a6ec5d2c7f44"),subQ5,subQ23,subQ9,subQ13,sQuery(id+"F0.wireOp",EDGE,"E37")])],"isStart":false})]})});}
            var sketch = newSketch(context, id + "F11", { "sketchPlane" : qUnion([Q0])});
            skLineSegment(sketch, "E61", {"start": v(21.5, -13.31) * mm, "end": v(-20.4, 13.29) * mm});
            skLineSegment(sketch, "E62", {"start": v(-20.4, 13.29) * mm, "end": v(-30.82, 19.9) * mm});
            skLineSegment(sketch, "E63", {"start": v(-30.82, 19.9) * mm, "end": v(11.27, 36.8) * mm});
            skLineSegment(sketch, "E64", {"start": v(11.27, 36.8) * mm, "end": v(29.43, 4.9) * mm});
            skLineSegment(sketch, "E65", {"start": v(29.43, 4.9) * mm, "end": v(29.43, -5.19) * mm});
            skCircle(sketch, "E66", {"center": v(6.48, 9.28) * mm, "radius": 27.13 * mm});
            skCircle(sketch, "E67", {"center": v(-5.33, -9.28) * mm, "radius": 27.13 * mm});
            skCircle(sketch, "E68", {"center": v(-5.33, -9.28) * mm, "radius": 35 * mm});
            skSolve(sketch);
        }
        {
            var Q0;
            {var subQ0=sQuery(id+"F11.wireOp",EDGE,"E64");var subQ1=sQuery(id+"F11.wireOp",EDGE,"E63");var subQ2=makeQuery(id+"F11.imprint","INTERSECT",VERTEX,{"derivedFrom":[subQ1,subQ0]});Q0=makeQuery(id+"F11.imprint","IMPRINT",FACE,{"disambiguationData":[TD([[makeQuery(id+"F11.imprint","IMPRINT",EDGE,{"disambiguationData":[TD([[subQ2,1.0]])],"derivedFrom":subQ1}),-1.0]])]});}
            var Q1;
            {var subQ3=sQuery(id+"F11.wireOp",EDGE,"E68");var subQ5=sQuery(id+"F11.wireOp",EDGE,"E66");var subQ6=makeQuery(id+"F11.imprint","INTERSECT",VERTEX,{"derivedFrom":[subQ5,subQ3]});Q1=makeQuery(id+"F11.imprint","IMPRINT",FACE,{"disambiguationData":[TD([[makeQuery(id+"F11.imprint","IMPRINT",EDGE,{"disambiguationData":[TD([[subQ6,-1.0]])],"derivedFrom":subQ5}),-1.0]])]});}
            var Q2;
            {var subQ0=sQuery(id+"F11.wireOp",EDGE,"E68");var subQ1=sQuery(id+"F11.wireOp",EDGE,"E66");var subQ2=makeQuery(id+"F11.imprint","INTERSECT",VERTEX,{"derivedFrom":[subQ1,subQ0]});Q2=makeQuery(id+"F11.imprint","IMPRINT",FACE,{"disambiguationData":[TD([[makeQuery(id+"F11.imprint","IMPRINT",EDGE,{"disambiguationData":[TD([[subQ2,-1.0]])],"derivedFrom":subQ1}),1.0]])]});}
            var Q3;
            {var subQ5=sQuery(id+"F0.wireOp",EDGE,"E13");var subQ6=makeQuery(id+"F1.opExtrude","CAP_EDGE",EDGE,{"disambiguationData":[OSD([subQ5]),TDD([makeQuery(id+"F0.imprint","IMPRINT",EDGE,{"disambiguationData":[TD([[makeQuery(id+"F0.imprint","INTERSECT",VERTEX,{"derivedFrom":[subQ5,sQuery(id+"F0.wireOp",EDGE,"E27")]}),1.0]])],"derivedFrom":subQ5})])],"isStart":false});Q3=makeQuery(id+"F11.imprint","IMPRINT",FACE,{"disambiguationData":[TD([[makeQuery(id+"F11.imprint","IMPRINT",EDGE,{"derivedFrom":subQ6}),-1.0]])]});}
            var Q4;
            {var subQ1=sQuery(id+"F11.wireOp",EDGE,"E66");var subQ2=sQuery(id+"F11.wireOp",EDGE,"E61");var subQ4=makeQuery(id+"F11.imprint","INTERSECT",VERTEX,{"derivedFrom":[subQ2,subQ1]});Q4=makeQuery(id+"F11.imprint","IMPRINT",FACE,{"disambiguationData":[TD([[makeQuery(id+"F11.imprint","IMPRINT",EDGE,{"disambiguationData":[TD([[subQ4,1.0]])],"derivedFrom":subQ1}),1.0]])]});}
            extrude(context, id + "F12", {"entities" : qUnion([Q0, Q1, Q2, Q3, Q4]), "operationType" : NewBodyOperationType.REMOVE, "oppositeDirection" : true, "depth" : 25 * mm, "offsetDistance" : 25 * mm});
        }
    });
